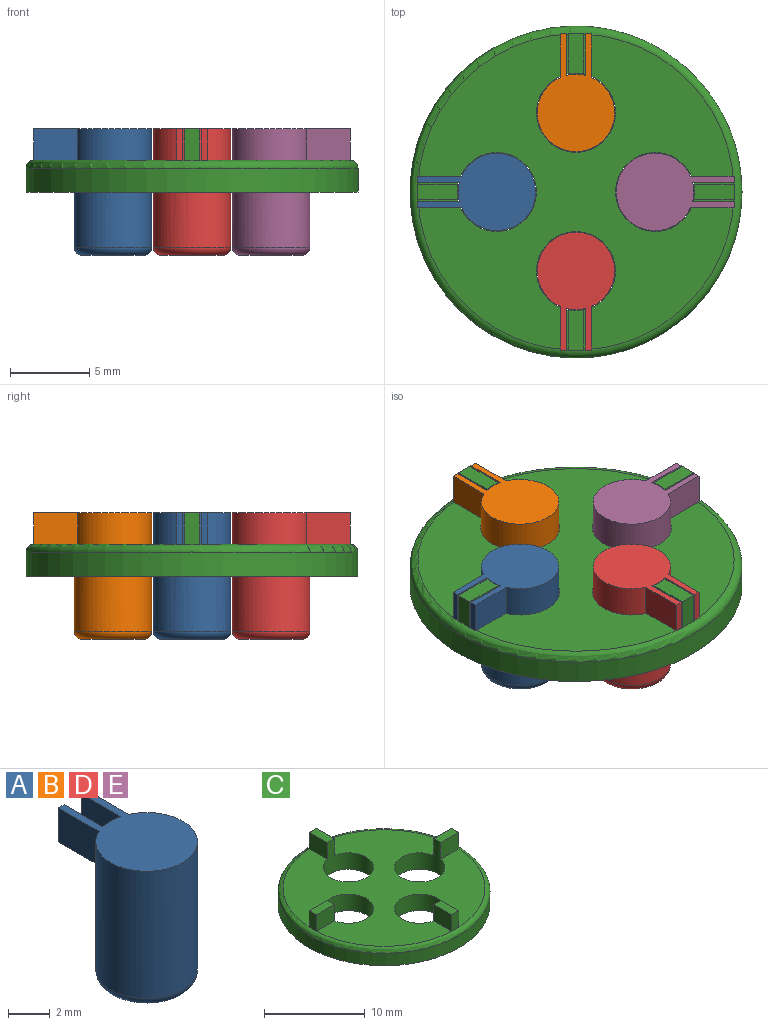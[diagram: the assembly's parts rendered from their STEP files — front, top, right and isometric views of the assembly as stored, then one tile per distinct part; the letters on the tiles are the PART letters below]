
ASSEMBLY  parts=5 mates=1
PART A: 12 faces, bbox 5.3x7.7x8 mm
  f0: cylinder r=2.45mm len=7.5mm, axis (0,0,-1), area 113.8mm2, adj f1,f3,f4,f6,f7,f8,f10,f11
  f1: plane 7.45x4.9mm, normal (0,0,1), area 21mm2, adj f0,f3,f4,f5,f7,f8,f9
  f2: plane 3.9x3.9mm, normal (0,0,-1), area 11.9mm2, adj f11
  f3: plane 2.62x2mm, normal (1,0,0), area 5.2mm2, adj f0,f1,f5,f6
  f4: plane 2.76x2mm, normal (-1,0,0), area 5.5mm2, adj f0,f1,f5,f6
  f5: plane 2x0.4mm, normal (0,1,0), area 0.8mm2, adj f1,f3,f4,f6
  f6: plane 2.76x0.4mm, normal (0,0,-1), area 1.1mm2, adj f0,f3,f4,f5
  f7: plane 2.62x2mm, normal (-1,0,0), area 5.2mm2, adj f0,f1,f9,f10
  f8: plane 2.76x2mm, normal (1,0,0), area 5.5mm2, adj f0,f1,f9,f10
  f9: plane 2x0.4mm, normal (0,1,0), area 0.8mm2, adj f1,f7,f8,f10
  f10: plane 2.76x0.4mm, normal (0,0,-1), area 1.1mm2, adj f0,f7,f8,f9
  f11: torus R=1.95mm, axis (0,0,1), area 11.2mm2, adj f0,f2
PART B: same geometry as A
PART C: 24 faces, bbox 22.7x22.7x4 mm
  f0: plane 19.98x19.98mm, normal (0,0,1), area 225.6mm2, adj f3,f4,f6,f8,f9,f11,f13,f14
  f1: cylinder r=10.5mm len=21mm, axis (0,0,-1), area 99mm2, adj f2,f23
  f2: plane 21x21mm, normal (0,0,-1), area 267.8mm2, adj f1,f3,f8,f13,f18
  f3: cylinder r=2.5mm len=5mm, axis (0,0,-1), area 33.4mm2, adj f0,f2,f4,f6,f7
  f4: plane 2.55x2mm, normal (1,0,0), area 5.1mm2, adj f0,f3,f5,f7,f23
  f5: plane 2.01x1.01mm, normal (0,1,0), area 2mm2, adj f4,f6,f7,f23
  f6: plane 2.55x2mm, normal (-1,0,0), area 5.1mm2, adj f0,f3,f5,f7,f23
  f7: plane 2.55x1mm, normal (0,0,1), area 2.5mm2, adj f3,f4,f5,f6
  f8: cylinder r=2.5mm len=5mm, axis (0,0,-1), area 33.4mm2, adj f0,f2,f9,f11,f12
  f9: plane 2.55x2mm, normal (0,-1,0), area 5.1mm2, adj f0,f8,f10,f12,f23
  f10: plane 2.01x1.01mm, normal (1,0,0), area 2mm2, adj f9,f11,f12,f23
  f11: plane 2.55x2mm, normal (0,1,0), area 5.1mm2, adj f0,f8,f10,f12,f23
  f12: plane 2.55x1mm, normal (0,0,1), area 2.5mm2, adj f8,f9,f10,f11
  f13: cylinder r=2.5mm len=5mm, axis (0,0,-1), area 33.4mm2, adj f0,f2,f14,f16,f17
  f14: plane 2.55x2mm, normal (-1,0,0), area 5.1mm2, adj f0,f13,f15,f17,f23
  f15: plane 2.01x1.01mm, normal (0,-1,0), area 2mm2, adj f14,f16,f17,f23
  f16: plane 2.55x2mm, normal (1,0,0), area 5.1mm2, adj f0,f13,f15,f17,f23
  f17: plane 2.55x1mm, normal (0,0,1), area 2.5mm2, adj f13,f14,f15,f16
  f18: cylinder r=2.5mm len=5mm, axis (0,0,-1), area 33.4mm2, adj f0,f2,f19,f21,f22
  f19: plane 2.55x2mm, normal (0,1,0), area 5.1mm2, adj f0,f18,f20,f22,f23
  f20: plane 2.01x1.01mm, normal (-1,0,0), area 2mm2, adj f19,f21,f22,f23
  f21: plane 2.55x2mm, normal (0,-1,0), area 5.1mm2, adj f0,f18,f20,f22,f23
  f22: plane 2.55x1mm, normal (0,0,1), area 2.5mm2, adj f18,f19,f20,f21
  f23: torus R=10mm, axis (0,0,1), area 50.9mm2, adj f0,f1,f4,f5,f6,f9,f10,f11
PART D: same geometry as A
PART E: same geometry as A
PLACE A rot(axis=(0,0,1),90deg) t=(-5,52.15,0.63)mm
PLACE B t=(52.15,5,0.63)mm
PLACE C t=(0,0,4.63)mm fixed
PLACE D rot(axis=(0,0,1),180deg) t=(-52.15,-5,0.63)mm
PLACE E rot(axis=(0,0,-1),90deg) t=(5,-52.15,0.63)mm
MATE slider B.f0 <-> C.f3  axis (0,0,1) through (0,5,0.63)mm
